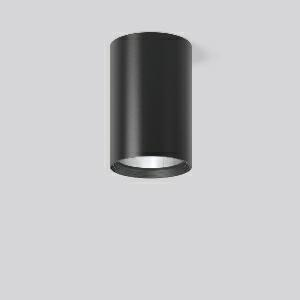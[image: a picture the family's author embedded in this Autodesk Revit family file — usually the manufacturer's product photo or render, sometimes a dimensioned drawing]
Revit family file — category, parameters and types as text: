
# Revit family: heledon_maxi_a_931217_003_3_b850
name_source: partatom
category: Lighting Fixtures
units: mm (PartAtom-declared; Revit-internal decimal feet)

## family parameters
Cut with Voids When Loaded = No
Host = Face
Light Source = No
Part Type = Normal
Room Calculation Point = No
Round Connector Dimension = Use Diameter
Shared = No

## types (1)
- HELEDON maxi A (1 x LED Modul 935, 3400 lm, 3500)
    Apparent Load = 25 VA
    Approval mark = CE
    CIE Flux Codes = 100 100 100 100 100
    Color Rendering = 92
    Color Temperature = 3500
    Default Elevation = 1800 mm
    Description = Series: HELEDON maxi
Cylindrical surface-mounted downlight. Housing: die-cast aluminium, powder-coated. Internal ceiling frame polycarbonate with bayonet mounting. Black plastic ring and recessed LED to prevent glare from the side. Optical assembly with reflector made of MIRO-Silver with 98% total light reflection for outstanding efficiency - can be changed without tools. Best colour rendering index Ra>90. Suitable for Ceiling mounting. Easy installation with a separate ceiling frame with bayonet mounting and plug connection. Driver integrated. Connected via plug-in connector. High quality converter without flickering and stroboscopic effect. The following accessories can be mounted without use of tools: interchangeable lenses, decorative glasses, honeycomb louvre, clear and frosted diffusers, white interchangeable plastic ring. 
Colour: deep black, matt (RAL 9005)
Diameter: 123 mm
Height: 183 mm
Lamp: LED
Socket: without socket
Colour temperature: 3500K
Colour rendering index (CRI): 92
System power: 25 W
Rated luminous flux: 3400 lm
Luminous efficiency: 136 lm/W
Control gear: Regulated power supply
Protection class: I
Type of protection: IP 20
    Height = 183 mm
    Lamp = 1 x LED Modul 935
    Lamp Light Flux = 3400 lm
    Lamp count = 1
    Length = 123 mm
    Lifetime = 50000 h
    Luminous efficacy = 136 lm/W
    Manufacturer = RZB
    ModVariant = No
    Model = 931217.003.3
    Mounting Place = Ceiling
    Mounting Type = Surface mounted
    Number of Poles = 1
    OnlyDefault = Yes
    Power Factor = 1
    Product Name = HELEDON maxi A
    Product group = Surface mounted downlights
    ProductGroupID = 302
    Protection Class = Protection class I
    Protection Degree = IP 20
    RLX_Detail_Level = 1
    RLX_Emergency_Light_Flux = 0 lm
    RLX_Emergency_Type = 0
    RLX_Emergency_Type_DB = No
    RlxData = <blob elided: 98201 chars, md5=afb1a5c3>
    Socket = socket
    Standby Power = 0 W
    System Light Flux = 3400 lm
    System Power = 25 W
    Type Comments = Product without accessories
    Type Image = 931192.003.jpg
    URL = http://relux.com
    VarID = ---
    Voltage = 230 V
    Voltage Range = 220-240 V
    Weight = 0.00 kg
    Width = 0 mm  [stored 0 ft]

note: [stored X ft] marks values corroborated as IEEE doubles in the binary element streams (Revit-internal decimal feet)

## geometry (parser evidence)
native form markers: Blend x4, Sweep x10
no freeform markers — native parametric forms only
